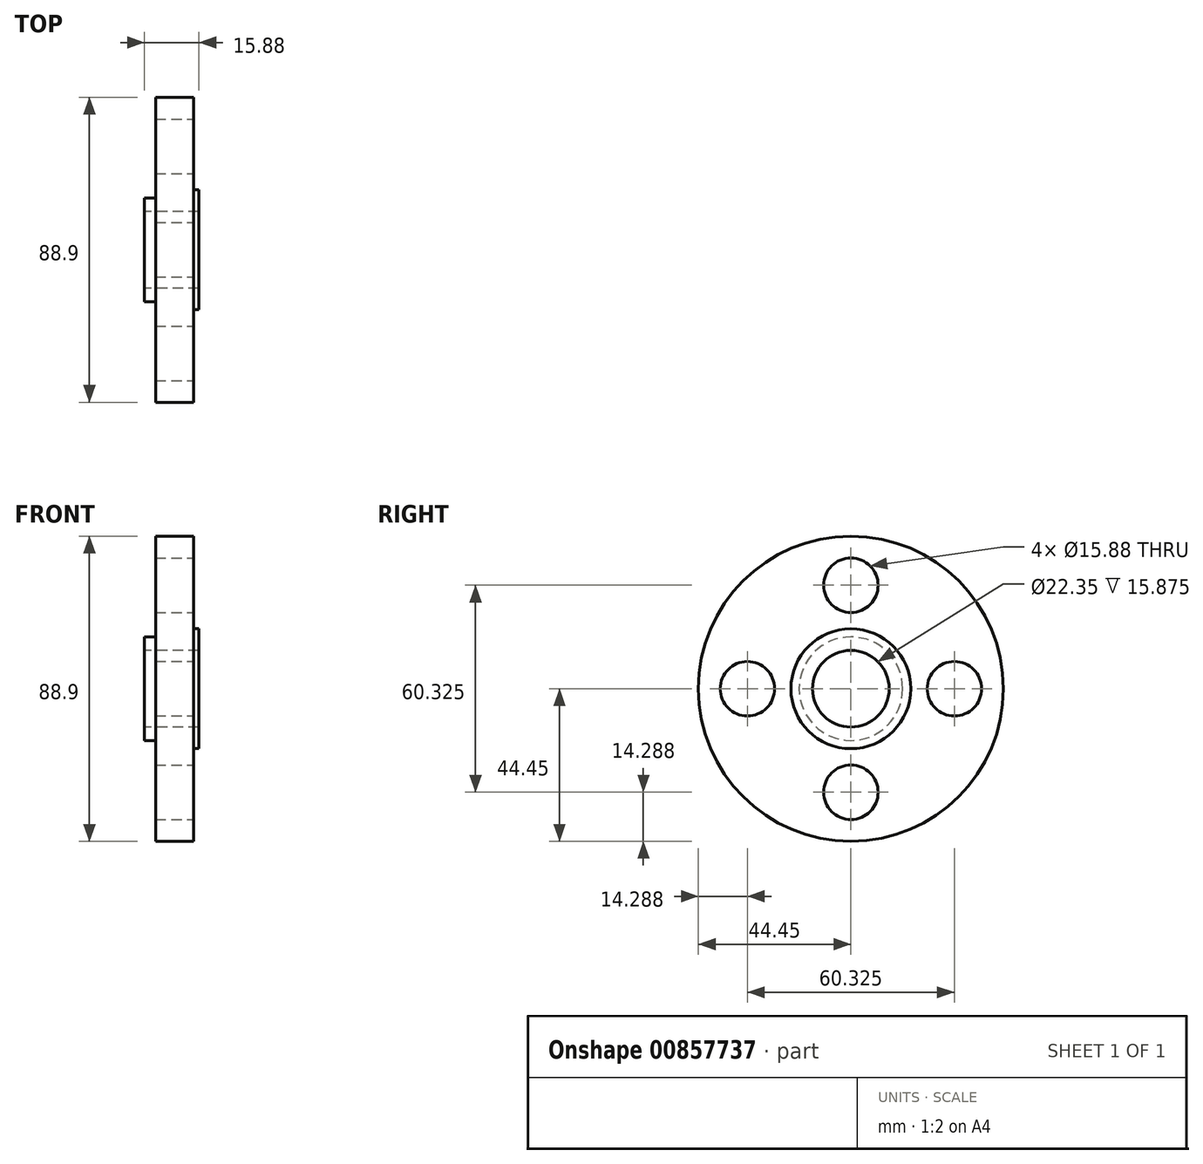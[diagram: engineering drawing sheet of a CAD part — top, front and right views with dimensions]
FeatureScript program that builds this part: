
annotation { "Feature Type Name" : "Feature", "Feature Type Description" : "" }
export const myFeature = defineFeature(function(context is Context, id is Id, definition is map)
    precondition{}
    {
        {
            var Q0;
            Q0=qCreatedBy(makeId("Front.planeOp"),FACE);
            var sketch = newSketch(context, id + "F0", { "sketchPlane" : qUnion([Q0])});
            skLineSegment(sketch, "E0", {"start": v(-31.71, 0) * mm, "end": v(27.5, 0) * mm, "construction": true});
            skLineSegment(sketch, "E1", {"start": v(0, 11.18) * mm, "end": v(15.88, 11.18) * mm});
            skLineSegment(sketch, "E2", {"start": v(15.88, 11.18) * mm, "end": v(15.88, 17.46) * mm});
            skLineSegment(sketch, "E3", {"start": v(15.88, 17.46) * mm, "end": v(14.35, 17.46) * mm});
            skLineSegment(sketch, "E4", {"start": v(14.35, 17.46) * mm, "end": v(14.35, 44.45) * mm});
            skLineSegment(sketch, "E5", {"start": v(14.35, 44.45) * mm, "end": v(3.25, 44.45) * mm});
            skLineSegment(sketch, "E6", {"start": v(3.25, 44.45) * mm, "end": v(3.25, 15.09) * mm});
            skLineSegment(sketch, "E7", {"start": v(3.25, 15.09) * mm, "end": v(0, 15.09) * mm});
            skLineSegment(sketch, "E8", {"start": v(0, 15.09) * mm, "end": v(0, 11.18) * mm});
            skSolve(sketch);
        }
        {
            var Q0;
            Q0 = qSketchRegion(id + "F0", true);
            var Q1;
            Q1=sQuery(id+"F0.wireOp",EDGE,"E0");
            revolve(context, id + "F1", {"surfaceOperationType" : NewSurfaceOperationType.NEW, "entities" : qUnion([Q0]), "axis" : qUnion([Q1]), "revolveType" : RevolveType.FULL});
        }
        {
            var Q0;
            Q0=makeQuery(id+"F1.opRevolve","SWEPT_FACE",FACE,{"disambiguationData":[OSD([sQuery(id+"F0.wireOp",EDGE,"E4")])]});
            var sketch = newSketch(context, id + "F2", { "sketchPlane" : qUnion([Q0])});
            skCircle(sketch, "E9", {"center": v(0, 0) * mm, "radius": 30.16 * mm, "construction": true});
            skCircle(sketch, "E10", {"center": v(0, 30.16) * mm, "radius": 7.94 * mm});
            skCircle(sketch, "E11.1.0", {"center": v(-30.16, 0) * mm, "radius": 7.94 * mm});
            skCircle(sketch, "E11.2.0", {"center": v(0, -30.16) * mm, "radius": 7.94 * mm});
            skCircle(sketch, "E11.3.0", {"center": v(30.16, 0) * mm, "radius": 7.94 * mm});
            skSolve(sketch);
        }
        {
            var Q0;
            Q0=makeQuery(id+"F2.imprint","IMPRINT",FACE,{"disambiguationData":[TD([[makeQuery(id+"F2.imprint","IMPRINT",EDGE,{"derivedFrom":sQuery(id+"F2.wireOp",EDGE,"E10")}),1.0]])]});
            var Q1;
            Q1=makeQuery(id+"F2.imprint","IMPRINT",FACE,{"disambiguationData":[TD([[makeQuery(id+"F2.imprint","IMPRINT",EDGE,{"derivedFrom":sQuery(id+"F2.wireOp",EDGE,"E11.3.0")}),1.0]])]});
            var Q2;
            Q2=makeQuery(id+"F2.imprint","IMPRINT",FACE,{"disambiguationData":[TD([[makeQuery(id+"F2.imprint","IMPRINT",EDGE,{"derivedFrom":sQuery(id+"F2.wireOp",EDGE,"E11.1.0")}),1.0]])]});
            var Q3;
            Q3=makeQuery(id+"F2.imprint","IMPRINT",FACE,{"disambiguationData":[TD([[makeQuery(id+"F2.imprint","IMPRINT",EDGE,{"derivedFrom":sQuery(id+"F2.wireOp",EDGE,"E11.2.0")}),1.0]])]});
            extrude(context, id + "F3", {"entities" : qUnion([Q0, Q1, Q2, Q3]), "operationType" : NewBodyOperationType.REMOVE, "oppositeDirection" : true, "depth" : 25.4 * mm, "offsetDistance" : 25.4 * mm});
        }
    });
